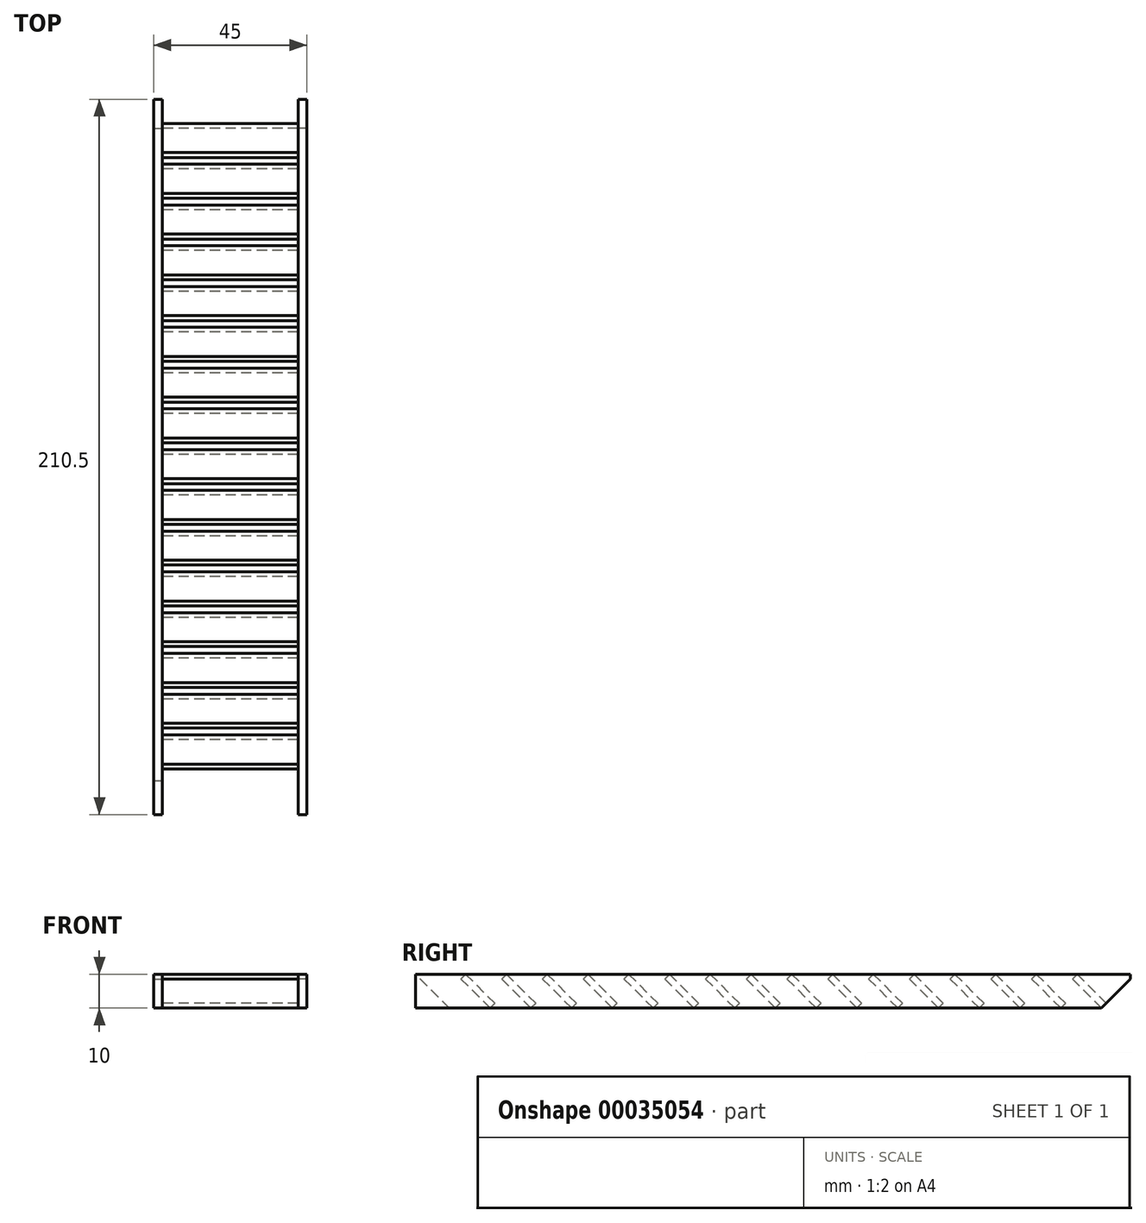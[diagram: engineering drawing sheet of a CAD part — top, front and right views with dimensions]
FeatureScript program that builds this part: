
annotation { "Feature Type Name" : "Feature", "Feature Type Description" : "" }
export const myFeature = defineFeature(function(context is Context, id is Id, definition is map)
    precondition{}
    {
        {
            var Q0;
            Q0=qCreatedBy(makeId("Top.planeOp"),FACE);
            var sketch = newSketch(context, id + "F0", { "sketchPlane" : qUnion([Q0])});
            skLineSegment(sketch, "E0.rect.bottom", {"start": v(22.5, -105.25) * mm, "end": v(-22.5, -105.25) * mm, "construction": true});
            skLineSegment(sketch, "E0.rect.top", {"start": v(22.5, 105.25) * mm, "end": v(-22.5, 105.25) * mm, "construction": true});
            skLineSegment(sketch, "E0.rect.left", {"start": v(22.5, -105.25) * mm, "end": v(22.5, 105.25) * mm, "construction": true});
            skLineSegment(sketch, "E0.rect.right", {"start": v(-22.5, -105.25) * mm, "end": v(-22.5, 105.25) * mm, "construction": true});
            skPoint(sketch, "E0.rect.middle", {"position": v(0, 0) * mm});
            skLineSegment(sketch, "E1.bottom", {"start": v(-22.5, -105.25) * mm, "end": v(-20, -105.25) * mm});
            skLineSegment(sketch, "E1.top", {"start": v(-22.5, 105.25) * mm, "end": v(-20, 105.25) * mm});
            skLineSegment(sketch, "E1.left", {"start": v(-22.5, -105.25) * mm, "end": v(-22.5, 105.25) * mm});
            skLineSegment(sketch, "E1.right", {"start": v(-20, -105.25) * mm, "end": v(-20, 105.25) * mm});
            skLineSegment(sketch, "E2.bottom", {"start": v(22.5, 105.25) * mm, "end": v(20, 105.25) * mm});
            skLineSegment(sketch, "E2.top", {"start": v(22.5, -105.25) * mm, "end": v(20, -105.25) * mm});
            skLineSegment(sketch, "E2.left", {"start": v(22.5, 105.25) * mm, "end": v(22.5, -105.25) * mm});
            skLineSegment(sketch, "E2.right", {"start": v(20, 105.25) * mm, "end": v(20, -105.25) * mm});
            skSolve(sketch);
        }
        {
            var Q0;
            Q0=qSketchRegion(id+"F0",true);
            extrude(context, id + "F1", {"entities" : qUnion([Q0]), "depth" : 10 * mm});
        }
        {
            var Q0;
            Q0=makeQuery(id+"F1.opExtrude","SWEPT_FACE",FACE,{"disambiguationData":[OSD([sQuery(id+"F0.wireOp",EDGE,"E1.right")])]});
            var sketch = newSketch(context, id + "F2", { "sketchPlane" : qUnion([Q0])});
            skLineSegment(sketch, "E3", {"start": v(-105.25, 0) * mm, "end": v(-95.25, 0) * mm});
            skLineSegment(sketch, "E4", {"start": v(-95.25, 0) * mm, "end": v(-105.25, 10) * mm});
            skLineSegment(sketch, "E5", {"start": v(-105.25, 10) * mm, "end": v(-105.25, 0) * mm});
            skLineSegment(sketch, "E6", {"start": v(-95.25, 0) * mm, "end": v(-83.25, 0) * mm, "construction": true});
            skLineSegment(sketch, "E7", {"start": v(-83.25, 0) * mm, "end": v(-93.25, 10) * mm, "construction": true});
            skLineSegment(sketch, "E8", {"start": v(-83.25, 0) * mm, "end": v(-81.84, 1.41) * mm});
            skLineSegment(sketch, "E9", {"start": v(-81.84, 1.41) * mm, "end": v(-90.42, 10) * mm});
            skLineSegment(sketch, "E10", {"start": v(-90.42, 10) * mm, "end": v(-91.84, 8.59) * mm});
            skLineSegment(sketch, "E11", {"start": v(-91.84, 8.59) * mm, "end": v(-83.25, 0) * mm});
            skLineSegment(sketch, "E12", {"start": v(-83.25, 0) * mm, "end": v(-71.25, 0) * mm, "construction": true});
            skLineSegment(sketch, "E13", {"start": v(-71.25, 0) * mm, "end": v(-81.25, 10) * mm, "construction": true});
            skLineSegment(sketch, "E14", {"start": v(-71.25, 0) * mm, "end": v(-69.84, 1.41) * mm});
            skLineSegment(sketch, "E15", {"start": v(-69.84, 1.41) * mm, "end": v(-78.42, 10) * mm});
            skLineSegment(sketch, "E16", {"start": v(-78.42, 10) * mm, "end": v(-79.84, 8.59) * mm});
            skLineSegment(sketch, "E17", {"start": v(-79.84, 8.59) * mm, "end": v(-71.25, 0) * mm});
            skLineSegment(sketch, "E18", {"start": v(-71.25, 0) * mm, "end": v(-59.25, 0) * mm, "construction": true});
            skLineSegment(sketch, "E19", {"start": v(-59.25, 0) * mm, "end": v(-69.25, 10) * mm, "construction": true});
            skLineSegment(sketch, "E20", {"start": v(-59.25, 0) * mm, "end": v(-57.84, 1.41) * mm});
            skLineSegment(sketch, "E21", {"start": v(-57.84, 1.41) * mm, "end": v(-66.42, 10) * mm});
            skLineSegment(sketch, "E22", {"start": v(-66.42, 10) * mm, "end": v(-67.84, 8.59) * mm});
            skLineSegment(sketch, "E23", {"start": v(-67.84, 8.59) * mm, "end": v(-59.25, 0) * mm});
            skLineSegment(sketch, "E24", {"start": v(-59.25, 0) * mm, "end": v(-47.25, 0) * mm, "construction": true});
            skLineSegment(sketch, "E25", {"start": v(-47.25, 0) * mm, "end": v(-57.25, 10) * mm, "construction": true});
            skLineSegment(sketch, "E26", {"start": v(-47.25, 0) * mm, "end": v(-45.84, 1.41) * mm});
            skLineSegment(sketch, "E27", {"start": v(-45.84, 1.41) * mm, "end": v(-54.42, 10) * mm});
            skLineSegment(sketch, "E28", {"start": v(-54.42, 10) * mm, "end": v(-55.84, 8.59) * mm});
            skLineSegment(sketch, "E29", {"start": v(-55.84, 8.59) * mm, "end": v(-47.25, 0) * mm});
            skLineSegment(sketch, "E30", {"start": v(-47.25, 0) * mm, "end": v(-35.25, 0) * mm, "construction": true});
            skLineSegment(sketch, "E31", {"start": v(-35.25, 0) * mm, "end": v(-45.25, 10) * mm, "construction": true});
            skLineSegment(sketch, "E32", {"start": v(-35.25, 0) * mm, "end": v(-33.84, 1.41) * mm});
            skLineSegment(sketch, "E33", {"start": v(-33.84, 1.41) * mm, "end": v(-42.42, 10) * mm});
            skLineSegment(sketch, "E34", {"start": v(-42.42, 10) * mm, "end": v(-43.84, 8.59) * mm});
            skLineSegment(sketch, "E35", {"start": v(-43.84, 8.59) * mm, "end": v(-35.25, 0) * mm});
            skLineSegment(sketch, "E36", {"start": v(-35.25, 0) * mm, "end": v(-23.25, 0) * mm, "construction": true});
            skLineSegment(sketch, "E37", {"start": v(-23.25, 0) * mm, "end": v(-33.25, 10) * mm, "construction": true});
            skLineSegment(sketch, "E38", {"start": v(-23.25, 0) * mm, "end": v(-21.84, 1.41) * mm});
            skLineSegment(sketch, "E39", {"start": v(-21.84, 1.41) * mm, "end": v(-30.42, 10) * mm});
            skLineSegment(sketch, "E40", {"start": v(-30.42, 10) * mm, "end": v(-31.84, 8.59) * mm});
            skLineSegment(sketch, "E41", {"start": v(-31.84, 8.59) * mm, "end": v(-23.25, 0) * mm});
            skLineSegment(sketch, "E42", {"start": v(-23.25, 0) * mm, "end": v(-11.25, 0) * mm, "construction": true});
            skLineSegment(sketch, "E43", {"start": v(-11.25, 0) * mm, "end": v(-21.25, 10) * mm, "construction": true});
            skLineSegment(sketch, "E44", {"start": v(-11.25, 0) * mm, "end": v(-9.84, 1.41) * mm});
            skLineSegment(sketch, "E45", {"start": v(-9.84, 1.41) * mm, "end": v(-18.42, 10) * mm});
            skLineSegment(sketch, "E46", {"start": v(-18.42, 10) * mm, "end": v(-19.84, 8.59) * mm});
            skLineSegment(sketch, "E47", {"start": v(-19.84, 8.59) * mm, "end": v(-11.25, 0) * mm});
            skLineSegment(sketch, "E48", {"start": v(-11.25, 0) * mm, "end": v(0.75, 0) * mm, "construction": true});
            skLineSegment(sketch, "E49", {"start": v(0.75, 0) * mm, "end": v(-9.25, 10) * mm, "construction": true});
            skLineSegment(sketch, "E50", {"start": v(0.75, 0) * mm, "end": v(2.16, 1.41) * mm});
            skLineSegment(sketch, "E51", {"start": v(2.16, 1.41) * mm, "end": v(-6.42, 10) * mm});
            skLineSegment(sketch, "E52", {"start": v(-6.42, 10) * mm, "end": v(-7.84, 8.59) * mm});
            skLineSegment(sketch, "E53", {"start": v(-7.84, 8.59) * mm, "end": v(0.75, 0) * mm});
            skLineSegment(sketch, "E54", {"start": v(0.75, 0) * mm, "end": v(12.75, 0) * mm, "construction": true});
            skLineSegment(sketch, "E55", {"start": v(12.75, 0) * mm, "end": v(2.75, 10) * mm, "construction": true});
            skLineSegment(sketch, "E56", {"start": v(12.75, 0) * mm, "end": v(14.16, 1.41) * mm});
            skLineSegment(sketch, "E57", {"start": v(14.16, 1.41) * mm, "end": v(5.58, 10) * mm});
            skLineSegment(sketch, "E58", {"start": v(5.58, 10) * mm, "end": v(4.16, 8.59) * mm});
            skLineSegment(sketch, "E59", {"start": v(4.16, 8.59) * mm, "end": v(12.75, 0) * mm});
            skLineSegment(sketch, "E60", {"start": v(12.75, 0) * mm, "end": v(24.75, 0) * mm, "construction": true});
            skLineSegment(sketch, "E61", {"start": v(24.75, 0) * mm, "end": v(14.75, 10) * mm, "construction": true});
            skLineSegment(sketch, "E62", {"start": v(24.75, 0) * mm, "end": v(26.16, 1.41) * mm});
            skLineSegment(sketch, "E63", {"start": v(26.16, 1.41) * mm, "end": v(17.58, 10) * mm});
            skLineSegment(sketch, "E64", {"start": v(17.58, 10) * mm, "end": v(16.16, 8.59) * mm});
            skLineSegment(sketch, "E65", {"start": v(16.16, 8.59) * mm, "end": v(24.75, 0) * mm});
            skLineSegment(sketch, "E66", {"start": v(24.75, 0) * mm, "end": v(36.75, 0) * mm, "construction": true});
            skLineSegment(sketch, "E67", {"start": v(36.75, 0) * mm, "end": v(26.75, 10) * mm, "construction": true});
            skLineSegment(sketch, "E68", {"start": v(36.75, 0) * mm, "end": v(38.16, 1.41) * mm});
            skLineSegment(sketch, "E69", {"start": v(38.16, 1.41) * mm, "end": v(29.58, 10) * mm});
            skLineSegment(sketch, "E70", {"start": v(29.58, 10) * mm, "end": v(28.16, 8.59) * mm});
            skLineSegment(sketch, "E71", {"start": v(28.16, 8.59) * mm, "end": v(36.75, 0) * mm});
            skLineSegment(sketch, "E72", {"start": v(36.75, 0) * mm, "end": v(48.75, 0) * mm, "construction": true});
            skLineSegment(sketch, "E73", {"start": v(48.75, 0) * mm, "end": v(38.75, 10) * mm, "construction": true});
            skLineSegment(sketch, "E74", {"start": v(48.75, 0) * mm, "end": v(50.16, 1.41) * mm});
            skLineSegment(sketch, "E75", {"start": v(50.16, 1.41) * mm, "end": v(41.58, 10) * mm});
            skLineSegment(sketch, "E76", {"start": v(41.58, 10) * mm, "end": v(40.16, 8.59) * mm});
            skLineSegment(sketch, "E77", {"start": v(40.16, 8.59) * mm, "end": v(48.75, 0) * mm});
            skLineSegment(sketch, "E78", {"start": v(48.75, 0) * mm, "end": v(60.75, 0) * mm, "construction": true});
            skLineSegment(sketch, "E79", {"start": v(60.75, 0) * mm, "end": v(50.75, 10) * mm, "construction": true});
            skLineSegment(sketch, "E80", {"start": v(60.75, 0) * mm, "end": v(62.16, 1.41) * mm});
            skLineSegment(sketch, "E81", {"start": v(62.16, 1.41) * mm, "end": v(53.58, 10) * mm});
            skLineSegment(sketch, "E82", {"start": v(53.58, 10) * mm, "end": v(52.16, 8.59) * mm});
            skLineSegment(sketch, "E83", {"start": v(52.16, 8.59) * mm, "end": v(60.75, 0) * mm});
            skLineSegment(sketch, "E84", {"start": v(60.75, 0) * mm, "end": v(72.75, 0) * mm, "construction": true});
            skLineSegment(sketch, "E85", {"start": v(72.75, 0) * mm, "end": v(62.75, 10) * mm, "construction": true});
            skLineSegment(sketch, "E86", {"start": v(72.75, 0) * mm, "end": v(74.16, 1.41) * mm});
            skLineSegment(sketch, "E87", {"start": v(74.16, 1.41) * mm, "end": v(65.58, 10) * mm});
            skLineSegment(sketch, "E88", {"start": v(65.58, 10) * mm, "end": v(64.16, 8.59) * mm});
            skLineSegment(sketch, "E89", {"start": v(64.16, 8.59) * mm, "end": v(72.75, 0) * mm});
            skLineSegment(sketch, "E90", {"start": v(72.75, 0) * mm, "end": v(84.75, 0) * mm, "construction": true});
            skLineSegment(sketch, "E91", {"start": v(84.75, 0) * mm, "end": v(74.75, 10) * mm, "construction": true});
            skLineSegment(sketch, "E92", {"start": v(84.75, 0) * mm, "end": v(86.16, 1.41) * mm});
            skLineSegment(sketch, "E93", {"start": v(86.16, 1.41) * mm, "end": v(77.58, 10) * mm});
            skLineSegment(sketch, "E94", {"start": v(77.58, 10) * mm, "end": v(76.16, 8.59) * mm});
            skLineSegment(sketch, "E95", {"start": v(76.16, 8.59) * mm, "end": v(84.75, 0) * mm});
            skLineSegment(sketch, "E96", {"start": v(84.75, 0) * mm, "end": v(96.75, 0) * mm, "construction": true});
            skLineSegment(sketch, "E97", {"start": v(96.75, 0) * mm, "end": v(86.75, 10) * mm, "construction": true});
            skLineSegment(sketch, "E98", {"start": v(96.75, 0) * mm, "end": v(98.16, 1.41) * mm});
            skLineSegment(sketch, "E99", {"start": v(98.16, 1.41) * mm, "end": v(89.58, 10) * mm});
            skLineSegment(sketch, "E100", {"start": v(89.58, 10) * mm, "end": v(88.16, 8.59) * mm});
            skLineSegment(sketch, "E101", {"start": v(88.16, 8.59) * mm, "end": v(96.75, 0) * mm});
            skLineSegment(sketch, "E102", {"start": v(96.75, 0) * mm, "end": v(105.25, 8.5) * mm});
            skLineSegment(sketch, "E103", {"start": v(105.25, 8.5) * mm, "end": v(105.25, 0) * mm});
            skLineSegment(sketch, "E104", {"start": v(105.25, 0) * mm, "end": v(96.75, 0) * mm});
            skSolve(sketch);
        }
        {
            var Q0;
            Q0=makeQuery(id+"F2.imprint","IMPRINT",FACE,{"disambiguationData":[TD([[makeQuery(id+"F2.imprint","IMPRINT",EDGE,{"derivedFrom":sQuery(id+"F2.wireOp",EDGE,"E8")}),1.0]])]});
            var Q1;
            Q1=makeQuery(id+"F2.imprint","IMPRINT",FACE,{"disambiguationData":[TD([[makeQuery(id+"F2.imprint","IMPRINT",EDGE,{"derivedFrom":sQuery(id+"F2.wireOp",EDGE,"E14")}),1.0]])]});
            var Q2;
            Q2=makeQuery(id+"F2.imprint","IMPRINT",FACE,{"disambiguationData":[TD([[makeQuery(id+"F2.imprint","IMPRINT",EDGE,{"derivedFrom":sQuery(id+"F2.wireOp",EDGE,"E20")}),1.0]])]});
            var Q3;
            Q3=makeQuery(id+"F2.imprint","IMPRINT",FACE,{"disambiguationData":[TD([[makeQuery(id+"F2.imprint","IMPRINT",EDGE,{"derivedFrom":sQuery(id+"F2.wireOp",EDGE,"E26")}),1.0]])]});
            var Q4;
            Q4=makeQuery(id+"F2.imprint","IMPRINT",FACE,{"disambiguationData":[TD([[makeQuery(id+"F2.imprint","IMPRINT",EDGE,{"derivedFrom":sQuery(id+"F2.wireOp",EDGE,"E32")}),1.0]])]});
            var Q5;
            Q5=makeQuery(id+"F2.imprint","IMPRINT",FACE,{"disambiguationData":[TD([[makeQuery(id+"F2.imprint","IMPRINT",EDGE,{"derivedFrom":sQuery(id+"F2.wireOp",EDGE,"E38")}),1.0]])]});
            var Q6;
            Q6=makeQuery(id+"F2.imprint","IMPRINT",FACE,{"disambiguationData":[TD([[makeQuery(id+"F2.imprint","IMPRINT",EDGE,{"derivedFrom":sQuery(id+"F2.wireOp",EDGE,"E44")}),1.0]])]});
            var Q7;
            Q7=makeQuery(id+"F2.imprint","IMPRINT",FACE,{"disambiguationData":[TD([[makeQuery(id+"F2.imprint","IMPRINT",EDGE,{"derivedFrom":sQuery(id+"F2.wireOp",EDGE,"E50")}),1.0]])]});
            var Q8;
            Q8=makeQuery(id+"F2.imprint","IMPRINT",FACE,{"disambiguationData":[TD([[makeQuery(id+"F2.imprint","IMPRINT",EDGE,{"derivedFrom":sQuery(id+"F2.wireOp",EDGE,"E56")}),1.0]])]});
            var Q9;
            Q9=makeQuery(id+"F2.imprint","IMPRINT",FACE,{"disambiguationData":[TD([[makeQuery(id+"F2.imprint","IMPRINT",EDGE,{"derivedFrom":sQuery(id+"F2.wireOp",EDGE,"E62")}),1.0]])]});
            var Q10;
            Q10=makeQuery(id+"F2.imprint","IMPRINT",FACE,{"disambiguationData":[TD([[makeQuery(id+"F2.imprint","IMPRINT",EDGE,{"derivedFrom":sQuery(id+"F2.wireOp",EDGE,"E68")}),1.0]])]});
            var Q11;
            Q11=makeQuery(id+"F2.imprint","IMPRINT",FACE,{"disambiguationData":[TD([[makeQuery(id+"F2.imprint","IMPRINT",EDGE,{"derivedFrom":sQuery(id+"F2.wireOp",EDGE,"E74")}),1.0]])]});
            var Q12;
            Q12=makeQuery(id+"F2.imprint","IMPRINT",FACE,{"disambiguationData":[TD([[makeQuery(id+"F2.imprint","IMPRINT",EDGE,{"derivedFrom":sQuery(id+"F2.wireOp",EDGE,"E80")}),1.0]])]});
            var Q13;
            Q13=makeQuery(id+"F2.imprint","IMPRINT",FACE,{"disambiguationData":[TD([[makeQuery(id+"F2.imprint","IMPRINT",EDGE,{"derivedFrom":sQuery(id+"F2.wireOp",EDGE,"E86")}),1.0]])]});
            var Q14;
            Q14=makeQuery(id+"F2.imprint","IMPRINT",FACE,{"disambiguationData":[TD([[makeQuery(id+"F2.imprint","IMPRINT",EDGE,{"derivedFrom":sQuery(id+"F2.wireOp",EDGE,"E92")}),1.0]])]});
            var Q15;
            {var subQ2=sQuery(id+"F2.wireOp",EDGE,"E99");Q15=makeQuery(id+"F2.imprint","IMPRINT",FACE,{"disambiguationData":[TD([[makeQuery(id+"F2.imprint","IMPRINT",EDGE,{"derivedFrom":subQ2}),1.0]])]});}
            extrude(context, id + "F3", {"entities" : qUnion([Q0, Q1, Q2, Q3, Q4, Q5, Q6, Q7, Q8, Q9, Q10, Q11, Q12, Q13, Q14, Q15]), "operationType" : NewBodyOperationType.ADD, "depth" : 41 * mm});
        }
        {
            var Q0;
            {var subQ1=sQuery(id+"F2.wireOp",EDGE,"E103");Q0=makeQuery(id+"F2.imprint","IMPRINT",FACE,{"disambiguationData":[TD([[makeQuery(id+"F2.imprint","IMPRINT",EDGE,{"derivedFrom":subQ1}),-1.0]])]});}
            var Q1;
            Q1=makeQuery(id+"F2.imprint","IMPRINT",FACE,{"disambiguationData":[TD([[makeQuery(id+"F2.imprint","IMPRINT",EDGE,{"derivedFrom":sQuery(id+"F2.wireOp",EDGE,"E3")}),1.0]])]});
            extrude(context, id + "F4", {"entities" : qUnion([Q0, Q1]), "operationType" : NewBodyOperationType.REMOVE, "oppositeDirection" : true, "depth" : 3 * mm});
        }
        {
            var Q0;
            Q0=makeQuery(id+"F1.opExtrude","SWEPT_FACE",FACE,{"disambiguationData":[OSD([sQuery(id+"F0.wireOp",EDGE,"E2.right")])]});
            var sketch = newSketch(context, id + "F5", { "sketchPlane" : qUnion([Q0])});
            skLineSegment(sketch, "E105", {"start": v(-105.25, 8.5) * mm, "end": v(-105.25, 0) * mm});
            skLineSegment(sketch, "E106", {"start": v(-105.25, 0) * mm, "end": v(-96.75, 0) * mm});
            skLineSegment(sketch, "E107", {"start": v(-96.75, 0) * mm, "end": v(-105.25, 8.5) * mm});
            skLineSegment(sketch, "E108", {"start": v(105.25, 0) * mm, "end": v(95.25, 0) * mm});
            skLineSegment(sketch, "E109", {"start": v(95.25, 0) * mm, "end": v(105.25, 10) * mm});
            skLineSegment(sketch, "E110", {"start": v(105.25, 10) * mm, "end": v(105.25, 0) * mm});
            skSolve(sketch);
        }
        {
            var Q0;
            Q0=makeQuery(id+"F5.imprint","IMPRINT",FACE,{"disambiguationData":[TD([[makeQuery(id+"F5.imprint","IMPRINT",EDGE,{"derivedFrom":sQuery(id+"F5.wireOp",EDGE,"E108")}),1.0]])]});
            var Q1;
            Q1=makeQuery(id+"F5.imprint","IMPRINT",FACE,{"disambiguationData":[TD([[makeQuery(id+"F5.imprint","IMPRINT",EDGE,{"derivedFrom":sQuery(id+"F5.wireOp",EDGE,"E105")}),1.0]])]});
            extrude(context, id + "F6", {"entities" : qUnion([Q0, Q1]), "operationType" : NewBodyOperationType.REMOVE, "oppositeDirection" : true, "depth" : 4 * mm});
        }
    });
